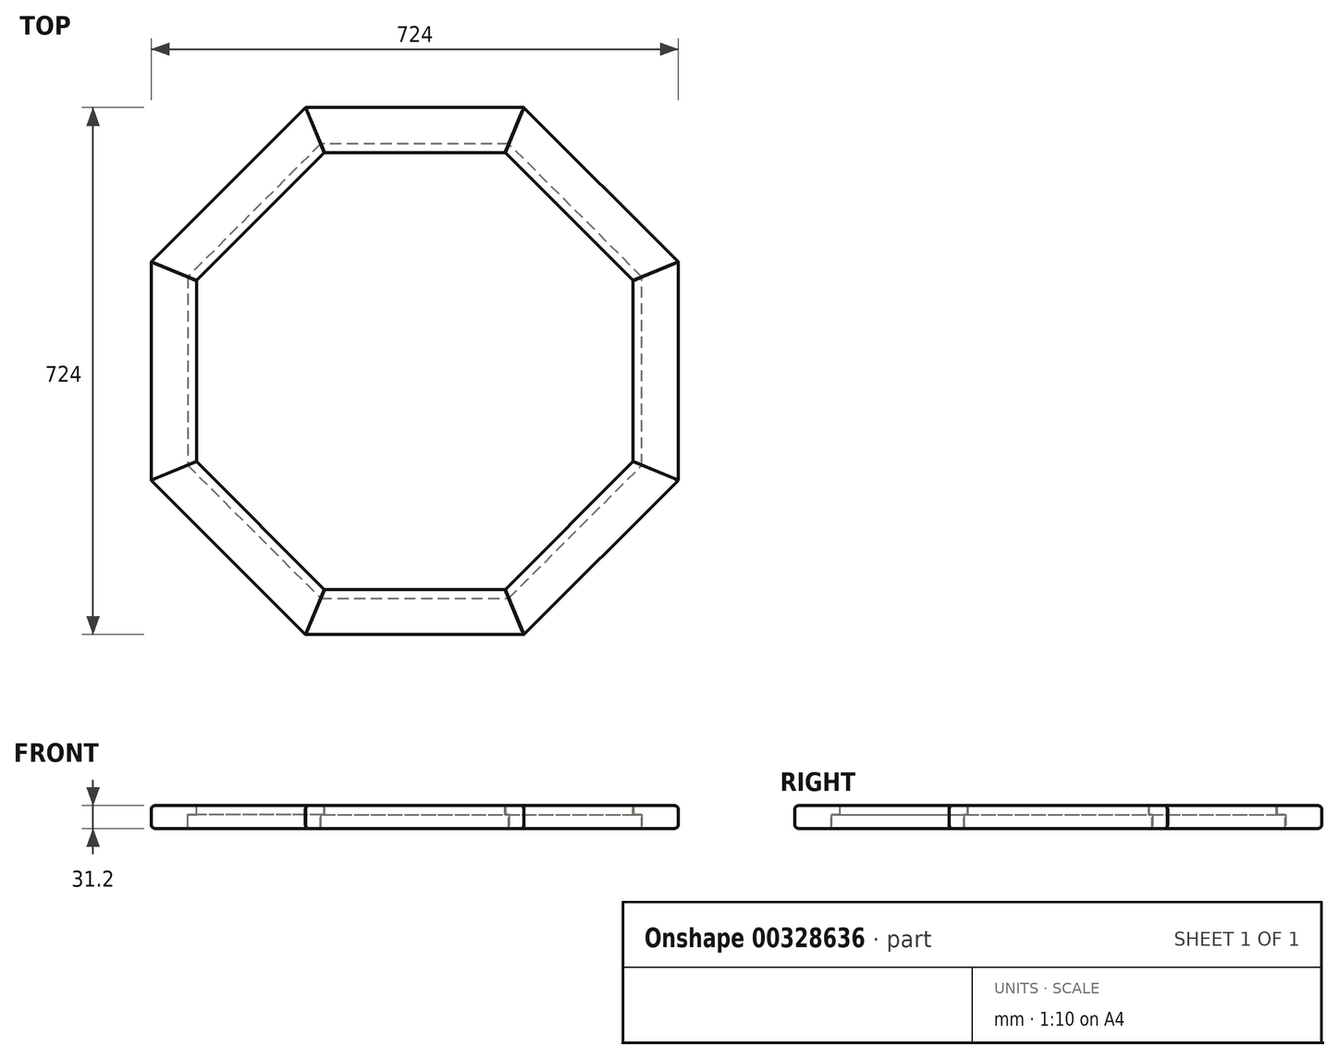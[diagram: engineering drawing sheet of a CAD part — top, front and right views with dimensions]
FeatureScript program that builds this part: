
annotation { "Feature Type Name" : "Feature", "Feature Type Description" : "" }
export const myFeature = defineFeature(function(context is Context, id is Id, definition is map)
    precondition{}
    {
        {
            var Q0;
            Q0=qCreatedBy(makeId("Top.planeOp"),FACE);
            var sketch = newSketch(context, id + "F0", { "sketchPlane" : qUnion([Q0])});
            skLineSegment(sketch, "E0.4", {"start": v(0, -362) * mm, "end": v(-149.95, -362) * mm});
            skLineSegment(sketch, "E1", {"start": v(-124.26, -300) * mm, "end": v(-149.95, -362) * mm});
            skLineSegment(sketch, "E2.0", {"start": v(0, -300) * mm, "end": v(-124.26, -300) * mm});
            skPoint(sketch, "E0.cCircle.center.orphan", {"position": v(0, 0) * mm});
            skLineSegment(sketch, "E3", {"start": v(0, 0) * mm, "end": v(-124.26, -300) * mm, "construction": true});
            skLineSegment(sketch, "E4", {"start": v(0, 0) * mm, "end": v(0, -300) * mm, "construction": true});
            skLineSegment(sketch, "E5", {"start": v(0, -300) * mm, "end": v(0, -362) * mm});
            skSolve(sketch);
        }
        {
            var Q0;
            Q0=qSketchRegion(id+"F0",true);
            extrude(context, id + "F1", {"entities" : qUnion([Q0]), "oppositeDirection" : true, "depth" : 31.2 * mm});
        }
        {
            var Q0;
            Q0=makeQuery(id+"F1.opExtrude","SWEPT_FACE",FACE,{"disambiguationData":[OSD([sQuery(id+"F0.wireOp",EDGE,"E5")])]});
            var sketch = newSketch(context, id + "F2", { "sketchPlane" : qUnion([Q0])});
            skLineSegment(sketch, "E6.bottom", {"start": v(-300, -31.2) * mm, "end": v(-312, -31.2) * mm});
            skLineSegment(sketch, "E6.top", {"start": v(-300, -12.5) * mm, "end": v(-312, -12.5) * mm});
            skLineSegment(sketch, "E6.left", {"start": v(-300, -31.2) * mm, "end": v(-300, -12.5) * mm});
            skLineSegment(sketch, "E6.right", {"start": v(-312, -31.2) * mm, "end": v(-312, -12.5) * mm});
            skSolve(sketch);
        }
        {
            var Q0;
            Q0=qSketchRegion(id+"F2",true);
            extrude(context, id + "F3", {"entities" : qUnion([Q0]), "operationType" : NewBodyOperationType.REMOVE, "endBound" : BoundingType.THROUGH_ALL, "oppositeDirection" : true, "depth" : 25 * mm});
        }
        {
            var Q0;
            Q0=makeQuery(id+"F1.opExtrude","CAP_EDGE",EDGE,{"disambiguationData":[OSD([sQuery(id+"F0.wireOp",EDGE,"E0.4")])],"isStart":true});
            var Q1;
            Q1=makeQuery(id+"F1.opExtrude","CAP_EDGE",EDGE,{"disambiguationData":[OSD([sQuery(id+"F0.wireOp",EDGE,"E0.4")])],"isStart":false});
            fillet(context, id + "F4", {"entities" : qUnion([Q0, Q1]), "radius" : 5 * mm, "tangentPropagation" : true, "allowEdgeOverflow" : false});
        }
        {
            var Q0;
            Q0=makeQuery(id+"F1.opExtrude","SWEPT_FACE",FACE,{"disambiguationData":[OSD([sQuery(id+"F0.wireOp",EDGE,"E1")])]});
            chamfer(context, id + "F5", {"entities" : qUnion([Q0]), "width" : .2 * mm, "tangentPropagation" : true});
        }
        {
            var Q0;
            Q0=makeQuery(id+"F1.opExtrude","SWEPT_BODY",BODY,{"disambiguationData":[OSD([sQuery(id+"F0.wireOp",EDGE,"E0.4"),sQuery(id+"F0.wireOp",EDGE,"E1"),sQuery(id+"F0.wireOp",EDGE,"E2.0"),sQuery(id+"F0.wireOp",EDGE,"E5")])]});
            var Q1;
            Q1=makeQuery(id+"F1.opExtrude","SWEPT_FACE",FACE,{"disambiguationData":[OSD([sQuery(id+"F0.wireOp",EDGE,"E5")])]});
            mirror(context, id + "F6", {"operationType" : NewBodyOperationType.ADD, "entities" : qUnion([Q0]), "mirrorPlane" : qUnion([Q1])});
        }
        {
            var Q0;
            Q0=qCreatedBy(makeId("Right.planeOp"),FACE);
            var sketch = newSketch(context, id + "F7", { "sketchPlane" : qUnion([Q0])});
            skLineSegment(sketch, "E7", {"start": v(0, 0) * mm, "end": v(0, 59.34) * mm, "construction": true});
            skSolve(sketch);
        }
        {
            var Q0;
            Q0=makeQuery(id+"F1.opExtrude","SWEPT_BODY",BODY,{"disambiguationData":[OSD([sQuery(id+"F0.wireOp",EDGE,"E0.4"),sQuery(id+"F0.wireOp",EDGE,"E1"),sQuery(id+"F0.wireOp",EDGE,"E2.0"),sQuery(id+"F0.wireOp",EDGE,"E5")])]});
            var Q1;
            Q1=sQuery(id+"F7.wireOp",EDGE,"E7");
            circularPattern(context, id + "F8", {"operationType" : NewBodyOperationType.ADD, "entities" : qUnion([Q0]), "axis" : qUnion([Q1]), "angle" : 360 * degree, "instanceCount" : 8, "equalSpace" : true});
        }
    });
